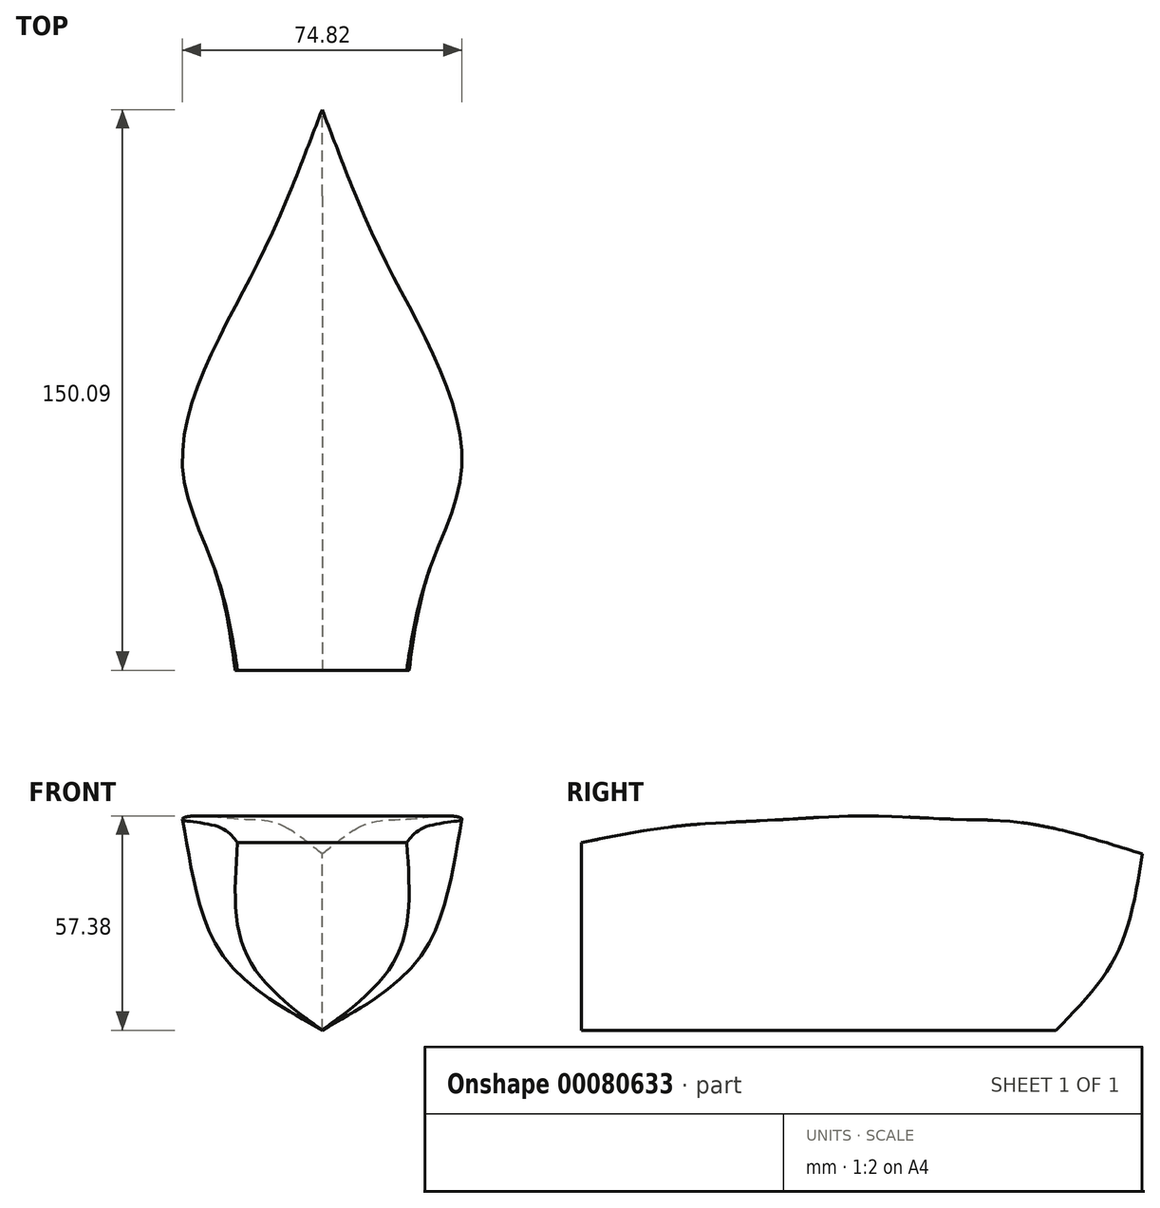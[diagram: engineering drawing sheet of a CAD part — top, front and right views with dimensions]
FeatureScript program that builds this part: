
annotation { "Feature Type Name" : "Feature", "Feature Type Description" : "" }
export const myFeature = defineFeature(function(context is Context, id is Id, definition is map)
    precondition{}
    {
        {
            var Q0;
            Q0=qCreatedBy(makeId("Front.planeOp"),FACE);
            var sketch = newSketch(context, id + "F0", { "sketchPlane" : qUnion([Q0])});
            skFitSpline(sketch, "E0", {"points": [v(0, 0) * mm, v(-5.66, 16.72) * mm, v(-9.04, 53.92) * mm], "startDerivative": vector(-15.55, 36.62) * mm, "endDerivative": vector(-3.3, 69.2) * mm});
            skSolve(sketch);
        }
        {
            var Q0;
            Q0=qCreatedBy(makeId("Front.planeOp"),FACE);
            cPlane(context, id + "F1", {"entities" : qUnion([Q0]), "cplaneType" : CPlaneType.OFFSET, "offset" : 25.4 * mm, "width" : 152.4 * mm, "height" : 152.4 * mm});
        }
        {
            var Q0;
            Q0=qCreatedBy(id+"F1.planeOp",FACE);
            var sketch = newSketch(context, id + "F2", { "sketchPlane" : qUnion([Q0])});
            skFitSpline(sketch, "E1", {"points": [v(0, 0) * mm, v(-12.08, 19.56) * mm, v(-21.08, 56.43) * mm], "startDerivative": vector(-30.14, 40.12) * mm, "endDerivative": vector(-12.73, 71.44) * mm});
            skSolve(sketch);
        }
        {
            var Q0;
            Q0=qCreatedBy(id+"F1.planeOp",FACE);
            cPlane(context, id + "F3", {"entities" : qUnion([Q0]), "cplaneType" : CPlaneType.OFFSET, "offset" : 25.4 * mm, "width" : 152.4 * mm, "height" : 152.4 * mm});
        }
        {
            var Q0;
            Q0=qCreatedBy(id+"F3.planeOp",FACE);
            var sketch = newSketch(context, id + "F4", { "sketchPlane" : qUnion([Q0])});
            skFitSpline(sketch, "E2", {"points": [v(0, 0) * mm, v(-18.24, 20.2) * mm, v(-33.25, 57.38) * mm], "startDerivative": vector(-43.32, 39.51) * mm, "endDerivative": vector(-23.81, 74.14) * mm});
            skSolve(sketch);
        }
        {
            var Q0;
            Q0=qCreatedBy(id+"F3.planeOp",FACE);
            cPlane(context, id + "F5", {"entities" : qUnion([Q0]), "cplaneType" : CPlaneType.OFFSET, "offset" : 25.4 * mm, "width" : 152.4 * mm, "height" : 152.4 * mm});
        }
        {
            var Q0;
            Q0=qCreatedBy(id+"F5.planeOp",FACE);
            var sketch = newSketch(context, id + "F6", { "sketchPlane" : qUnion([Q0])});
            skFitSpline(sketch, "E3", {"points": [v(0, 0) * mm, v(-27.02, 20.9) * mm, v(-36.95, 56.23) * mm], "startDerivative": vector(-63.74, 35.97) * mm, "endDerivative": vector(-10.47, 76.25) * mm});
            skSolve(sketch);
        }
        {
            var Q0;
            Q0=qCreatedBy(id+"F5.planeOp",FACE);
            cPlane(context, id + "F7", {"entities" : qUnion([Q0]), "cplaneType" : CPlaneType.OFFSET, "offset" : 25.4 * mm, "width" : 152.4 * mm, "height" : 152.4 * mm});
        }
        {
            var Q0;
            Q0=qCreatedBy(id+"F7.planeOp",FACE);
            var sketch = newSketch(context, id + "F8", { "sketchPlane" : qUnion([Q0])});
            skFitSpline(sketch, "E4", {"points": [v(0, 0) * mm, v(-23.78, 22.05) * mm, v(-28.17, 54.61) * mm], "startDerivative": vector(-57.43, 39.1) * mm, "endDerivative": vector(1.03, 70.1) * mm});
            skSolve(sketch);
        }
        {
            var Q0;
            Q0=qCreatedBy(id+"F7.planeOp",FACE);
            cPlane(context, id + "F9", {"entities" : qUnion([Q0]), "cplaneType" : CPlaneType.OFFSET, "offset" : 25.4 * mm, "width" : 152.4 * mm, "height" : 152.4 * mm});
        }
        {
            var Q0;
            Q0=qCreatedBy(id+"F9.planeOp",FACE);
            var sketch = newSketch(context, id + "F10", { "sketchPlane" : qUnion([Q0])});
            skFitSpline(sketch, "E5", {"points": [v(0, 0) * mm, v(-20.32, 20.44) * mm, v(-22.63, 50.22) * mm], "startDerivative": vector(-50.04, 36.83) * mm, "endDerivative": vector(4.61, 63.53) * mm});
            skSolve(sketch);
        }
        {
            var Q0;
            Q0=qCreatedBy(makeId("Right.planeOp"),FACE);
            var sketch = newSketch(context, id + "F11", { "sketchPlane" : qUnion([Q0])});
            skFitSpline(sketch, "E6", {"points": [v(0, 0) * mm, v(16.16, 20.2) * mm, v(23.1, 47.22) * mm], "startDerivative": vector(37.7, 38.27) * mm, "endDerivative": vector(8.67, 56.06) * mm});
            skSolve(sketch);
        }
        {
            var Q0;
            Q0=sQuery(id+"F11.wireOp",EDGE,"E6");
            var Q1;
            Q1=sQuery(id+"F0.wireOp",EDGE,"E0");
            var Q2;
            Q2=sQuery(id+"F2.wireOp",EDGE,"E1");
            var Q3;
            Q3=sQuery(id+"F4.wireOp",EDGE,"E2");
            var Q4;
            Q4=sQuery(id+"F6.wireOp",EDGE,"E3");
            var Q5;
            Q5=sQuery(id+"F8.wireOp",EDGE,"E4");
            var Q6;
            Q6=sQuery(id+"F10.wireOp",EDGE,"E5");
            loft(context, id + "F12", {"bodyType" : ToolBodyType.SURFACE, "wireProfilesArray" : [{ "wireProfileEntities" : qUnion([Q0]) }, { "wireProfileEntities" : qUnion([Q1]) }, { "wireProfileEntities" : qUnion([Q2]) }, { "wireProfileEntities" : qUnion([Q3]) }, { "wireProfileEntities" : qUnion([Q4]) }, { "wireProfileEntities" : qUnion([Q5]) }, { "wireProfileEntities" : qUnion([Q6]) }]});
        }
        {
            var Q0;
            Q0=makeQuery(id+"F12.opLoft","SWEPT_FACE",FACE,{"disambiguationData":[OSD([sQuery(id+"F0.wireOp",VERTEX,"E0.start"),sQuery(id+"F0.wireOp",VERTEX,"E0.end"),sQuery(id+"F0.wireOp",EDGE,"E0"),sQuery(id+"F2.wireOp",VERTEX,"E1.start"),sQuery(id+"F2.wireOp",VERTEX,"E1.end"),sQuery(id+"F2.wireOp",EDGE,"E1")])]});
            var Q1;
            Q1=makeQuery(id+"F12.opLoft","SWEPT_FACE",FACE,{"disambiguationData":[OSD([sQuery(id+"F0.wireOp",VERTEX,"E0.start"),sQuery(id+"F0.wireOp",VERTEX,"E0.end"),sQuery(id+"F0.wireOp",EDGE,"E0"),sQuery(id+"F11.wireOp",VERTEX,"E6.start"),sQuery(id+"F11.wireOp",VERTEX,"E6.end"),sQuery(id+"F11.wireOp",EDGE,"E6")])]});
            var Q2;
            Q2=qCreatedBy(makeId("Right.planeOp"),FACE);
            mirror(context, id + "F13", {"faces" : qUnion([Q0, Q1]), "mirrorPlane" : qUnion([Q2]), "patternType" : MirrorType.FACE});
        }
        {
            var Q0;
            Q0=makeQuery(id+"F13.opPattern","COPY",FACE,{"derivedFrom":makeQuery(id+"F12.opLoft","SWEPT_FACE",FACE,{"disambiguationData":[OSD([sQuery(id+"F0.wireOp",VERTEX,"E0.start"),sQuery(id+"F0.wireOp",VERTEX,"E0.end"),sQuery(id+"F0.wireOp",EDGE,"E0"),sQuery(id+"F2.wireOp",VERTEX,"E1.start"),sQuery(id+"F2.wireOp",VERTEX,"E1.end"),sQuery(id+"F2.wireOp",EDGE,"E1")])]}),"instanceName":"1"});
            var Q1;
            Q1=makeQuery(id+"F12.opLoft","SWEPT_FACE",FACE,{"disambiguationData":[OSD([sQuery(id+"F0.wireOp",VERTEX,"E0.start"),sQuery(id+"F0.wireOp",VERTEX,"E0.end"),sQuery(id+"F0.wireOp",EDGE,"E0"),sQuery(id+"F2.wireOp",VERTEX,"E1.start"),sQuery(id+"F2.wireOp",VERTEX,"E1.end"),sQuery(id+"F2.wireOp",EDGE,"E1")])]});
            loft(context, id + "F14", {"sheetProfilesArray" : [{ "sheetProfileEntities" : qUnion([Q0]) }, { "sheetProfileEntities" : qUnion([Q1]) }]});
        }
        {
            var Q1;
            Q1=makeQuery(id+"F12.opLoft","SWEPT_FACE",FACE,{"disambiguationData":[OSD([sQuery(id+"F0.wireOp",VERTEX,"E0.start"),sQuery(id+"F0.wireOp",VERTEX,"E0.end"),sQuery(id+"F0.wireOp",EDGE,"E0"),sQuery(id+"F11.wireOp",VERTEX,"E6.start"),sQuery(id+"F11.wireOp",VERTEX,"E6.end"),sQuery(id+"F11.wireOp",EDGE,"E6")])]});
            var Q2;
            Q2=makeQuery(id+"F13.opPattern","COPY",FACE,{"derivedFrom":makeQuery(id+"F12.opLoft","SWEPT_FACE",FACE,{"disambiguationData":[OSD([sQuery(id+"F0.wireOp",VERTEX,"E0.start"),sQuery(id+"F0.wireOp",VERTEX,"E0.end"),sQuery(id+"F0.wireOp",EDGE,"E0"),sQuery(id+"F11.wireOp",VERTEX,"E6.start"),sQuery(id+"F11.wireOp",VERTEX,"E6.end"),sQuery(id+"F11.wireOp",EDGE,"E6")])]}),"instanceName":"1"});
            loft(context, id + "F15", {"operationType" : NewBodyOperationType.ADD, "sheetProfilesArray" : [{ "sheetProfileEntities" : qUnion([Q1]) }, { "sheetProfileEntities" : qUnion([Q2]) }]});
        }
    });
